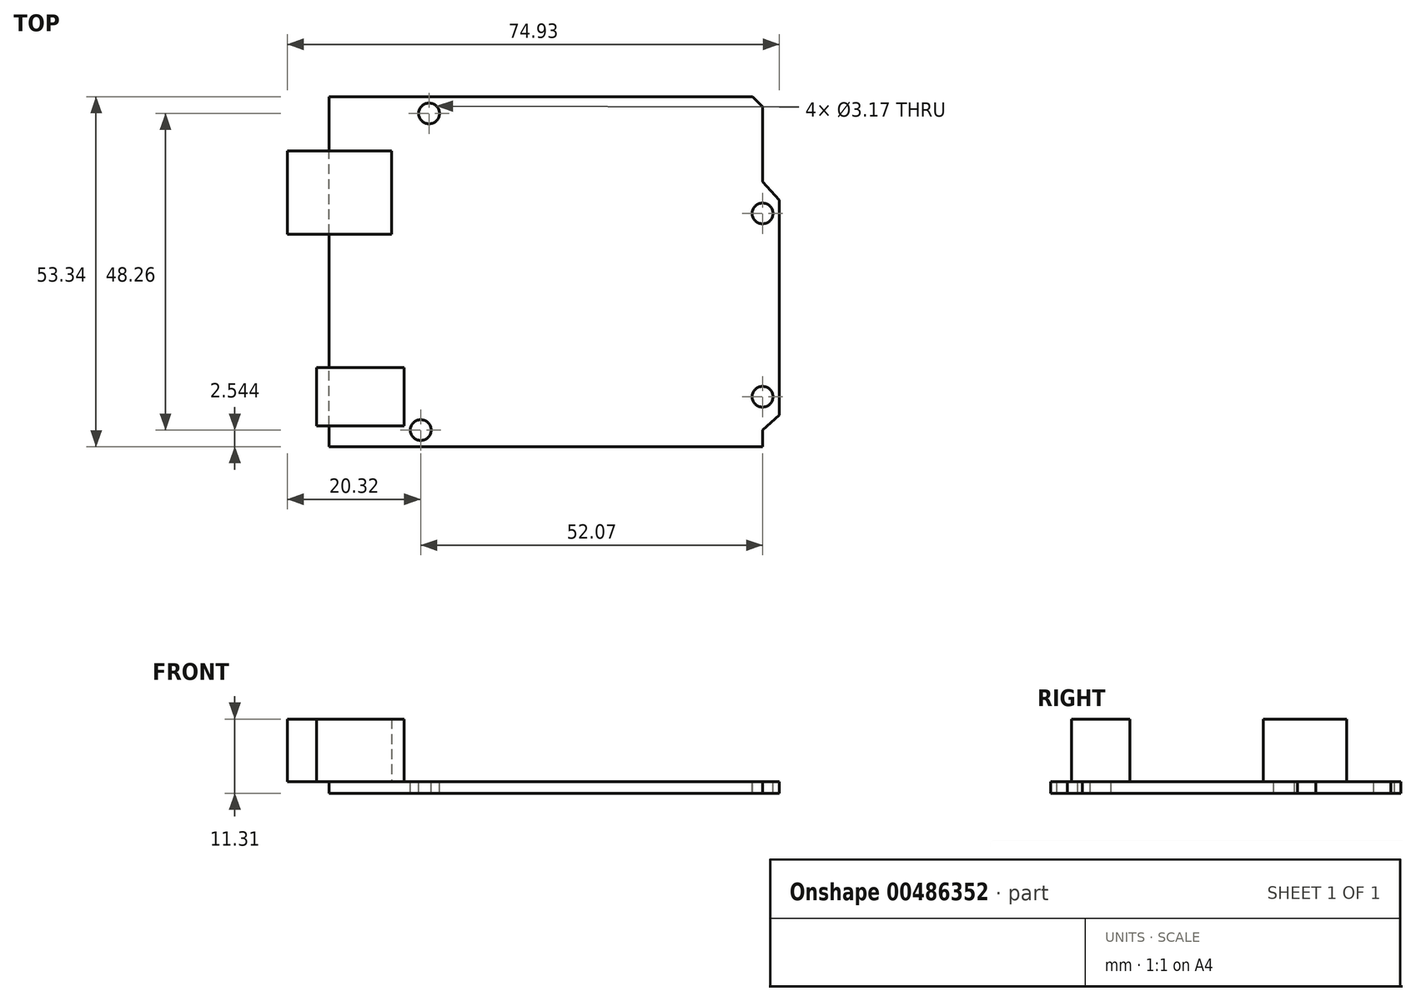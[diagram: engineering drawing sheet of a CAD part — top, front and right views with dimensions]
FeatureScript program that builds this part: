
annotation { "Feature Type Name" : "Feature", "Feature Type Description" : "" }
export const myFeature = defineFeature(function(context is Context, id is Id, definition is map)
    precondition{}
    {
        {
            var Q0;
            Q0=qCreatedBy(makeId("Top.planeOp"),FACE);
            var sketch = newSketch(context, id + "F0", { "sketchPlane" : qUnion([Q0])});
            skLineSegment(sketch, "E0", {"start": v(-66.04, -18.3) * mm, "end": v(-66.04, 35.03) * mm});
            skLineSegment(sketch, "E1", {"start": v(-66.04, 35.03) * mm, "end": v(-1.52, 35.03) * mm});
            skLineSegment(sketch, "E2", {"start": v(-66.04, -18.3) * mm, "end": v(0, -18.3) * mm});
            skLineSegment(sketch, "E3", {"start": v(0, -18.3) * mm, "end": v(0, -15.77) * mm});
            skLineSegment(sketch, "E4", {"start": v(-1.52, 35.03) * mm, "end": v(0, 33.5) * mm});
            skLineSegment(sketch, "E5", {"start": v(0, 33.5) * mm, "end": v(0, 22.08) * mm});
            skLineSegment(sketch, "E6", {"start": v(2.54, 19.3) * mm, "end": v(2.54, -13.47) * mm});
            skLineSegment(sketch, "E7", {"start": v(2.54, -13.47) * mm, "end": v(0, -15.77) * mm});
            skLineSegment(sketch, "E8", {"start": v(2.54, 19.3) * mm, "end": v(0, 22.08) * mm});
            skPoint(sketch, "E9.end.orphan", {"position": v(0, 13.44) * mm});
            skCircle(sketch, "E10", {"center": v(-50.8, 32.5) * mm, "radius": 1.59 * mm});
            skPoint(sketch, "E11.end.orphan", {"position": v(-47.08, 32.5) * mm});
            skPoint(sketch, "E12.end.orphan", {"position": v(-50.8, 28.93) * mm});
            skLineSegment(sketch, "E13", {"start": v(-52.83, -14.37) * mm, "end": v(-52.07, -14.37) * mm});
            skCircle(sketch, "E14", {"center": v(-52.07, -15.77) * mm, "radius": 1.59 * mm});
            skPoint(sketch, "E15.end.orphan", {"position": v(-44.12, -15.77) * mm});
            skCircle(sketch, "E16", {"center": v(0, 17.25) * mm, "radius": 1.59 * mm});
            skPoint(sketch, "E17.end.orphan", {"position": v(-6.66, 17.25) * mm});
            skLineSegment(sketch, "E18", {"start": v(-5.77, -18.3) * mm, "end": v(-5.77, -10.69) * mm});
            skCircle(sketch, "E19", {"center": v(0, -10.69) * mm, "radius": 1.59 * mm});
            skSolve(sketch);
        }
        {
            var Q0;
            Q0=qCreatedBy(makeId("Top.planeOp"),FACE);
            var sketch = newSketch(context, id + "F1", { "sketchPlane" : qUnion([Q0])});
            skLineSegment(sketch, "E20.bottom", {"start": v(-56.52, 14.08) * mm, "end": v(-72.4, 14.08) * mm});
            skLineSegment(sketch, "E20.top", {"start": v(-56.52, 26.78) * mm, "end": v(-72.4, 26.78) * mm});
            skLineSegment(sketch, "E20.left", {"start": v(-56.52, 14.08) * mm, "end": v(-56.52, 26.78) * mm});
            skLineSegment(sketch, "E20.right", {"start": v(-72.4, 14.08) * mm, "end": v(-72.4, 26.78) * mm});
            skLineSegment(sketch, "E21.bottom", {"start": v(-54.61, -15.13) * mm, "end": v(-67.95, -15.13) * mm});
            skLineSegment(sketch, "E21.top", {"start": v(-54.61, -6.24) * mm, "end": v(-67.95, -6.24) * mm});
            skLineSegment(sketch, "E21.left", {"start": v(-54.61, -15.13) * mm, "end": v(-54.61, -6.24) * mm});
            skLineSegment(sketch, "E22", {"start": v(-67.95, -6.24) * mm, "end": v(-67.95, -15.13) * mm});
            skPoint(sketch, "E21.right.end.orphan", {"position": v(-72.4, -6.24) * mm});
            skSolve(sketch);
        }
        {
            var Q0;
            Q0 = qSketchRegion(id + "F1", true);
            extrude(context, id + "F2", {"entities" : qUnion([Q0]), "depth" : 9.52 * mm, "offsetDistance" : 25.4 * mm});
        }
        {
            var Q0;
            Q0 = qSketchRegion(id + "F0", true);
            extrude(context, id + "F3", {"entities" : qUnion([Q0]), "depth" : -1.78 * mm, "offsetDistance" : 25.4 * mm});
        }
    });
